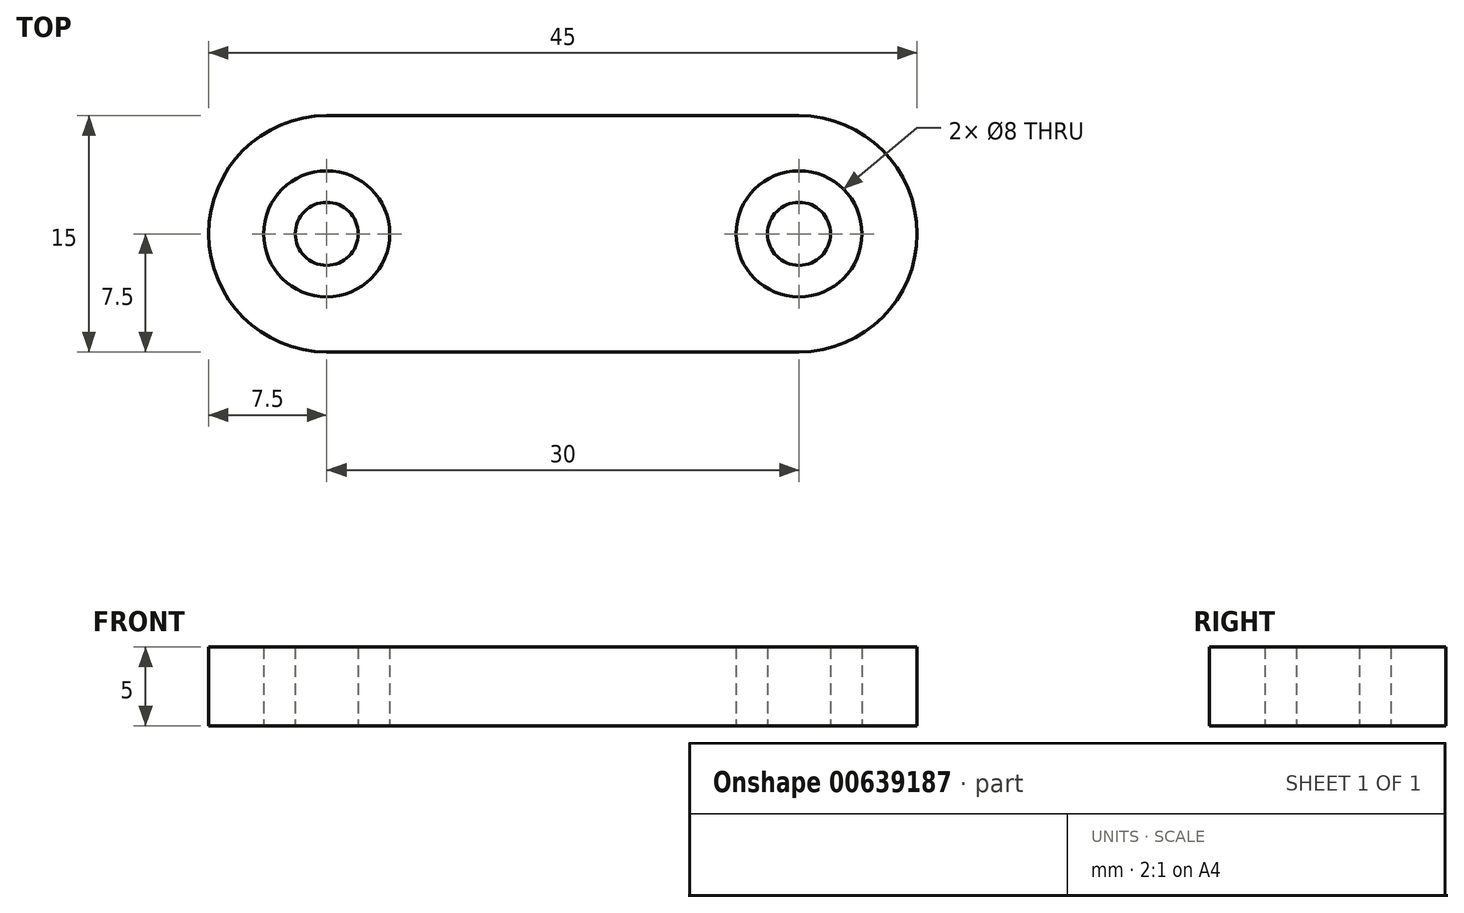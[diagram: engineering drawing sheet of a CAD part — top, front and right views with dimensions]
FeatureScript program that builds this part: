
annotation { "Feature Type Name" : "Feature", "Feature Type Description" : "" }
export const myFeature = defineFeature(function(context is Context, id is Id, definition is map)
    precondition{}
    {
        {
            var Q0;
            Q0=qCreatedBy(makeId("Top.planeOp"),FACE);
            var sketch = newSketch(context, id + "F0", { "sketchPlane" : qUnion([Q0])});
            skArc(sketch, "E0", {"start": v(0, 7.5) * mm, "mid": v(-7.5, 0) * mm, "end": v(0, -7.5) * mm});
            skArc(sketch, "E1", {"start": v(30, -7.5) * mm, "mid": v(37.5, 0) * mm, "end": v(30, 7.5) * mm});
            skLineSegment(sketch, "E2", {"start": v(0, 7.5) * mm, "end": v(30, 7.5) * mm});
            skLineSegment(sketch, "E3", {"start": v(0, -7.5) * mm, "end": v(30, -7.5) * mm});
            skCircle(sketch, "E4", {"center": v(0, 0) * mm, "radius": 4 * mm});
            skCircle(sketch, "E5", {"center": v(30, 0) * mm, "radius": 4 * mm});
            skSolve(sketch);
        }
        {
            var Q0;
            Q0 = qSketchRegion(id + "F0", true);
            extrude(context, id + "F1", {"entities" : qUnion([Q0]), "depth" : 5 * mm, "offsetDistance" : 25 * mm});
        }
        {
            var Q0;
            Q0=qCreatedBy(makeId("Top.planeOp"),FACE);
            var sketch = newSketch(context, id + "F2", { "sketchPlane" : qUnion([Q0])});
            skCircle(sketch, "E6", {"center": v(0, 0) * mm, "radius": 2 * mm});
            skCircle(sketch, "E7", {"center": v(30, 0) * mm, "radius": 2 * mm});
            skSolve(sketch);
        }
        {
            var Q0;
            Q0 = qSketchRegion(id + "F2", true);
            extrude(context, id + "F3", {"entities" : qUnion([Q0]), "depth" : 5 * mm, "offsetDistance" : 25 * mm});
        }
    });
